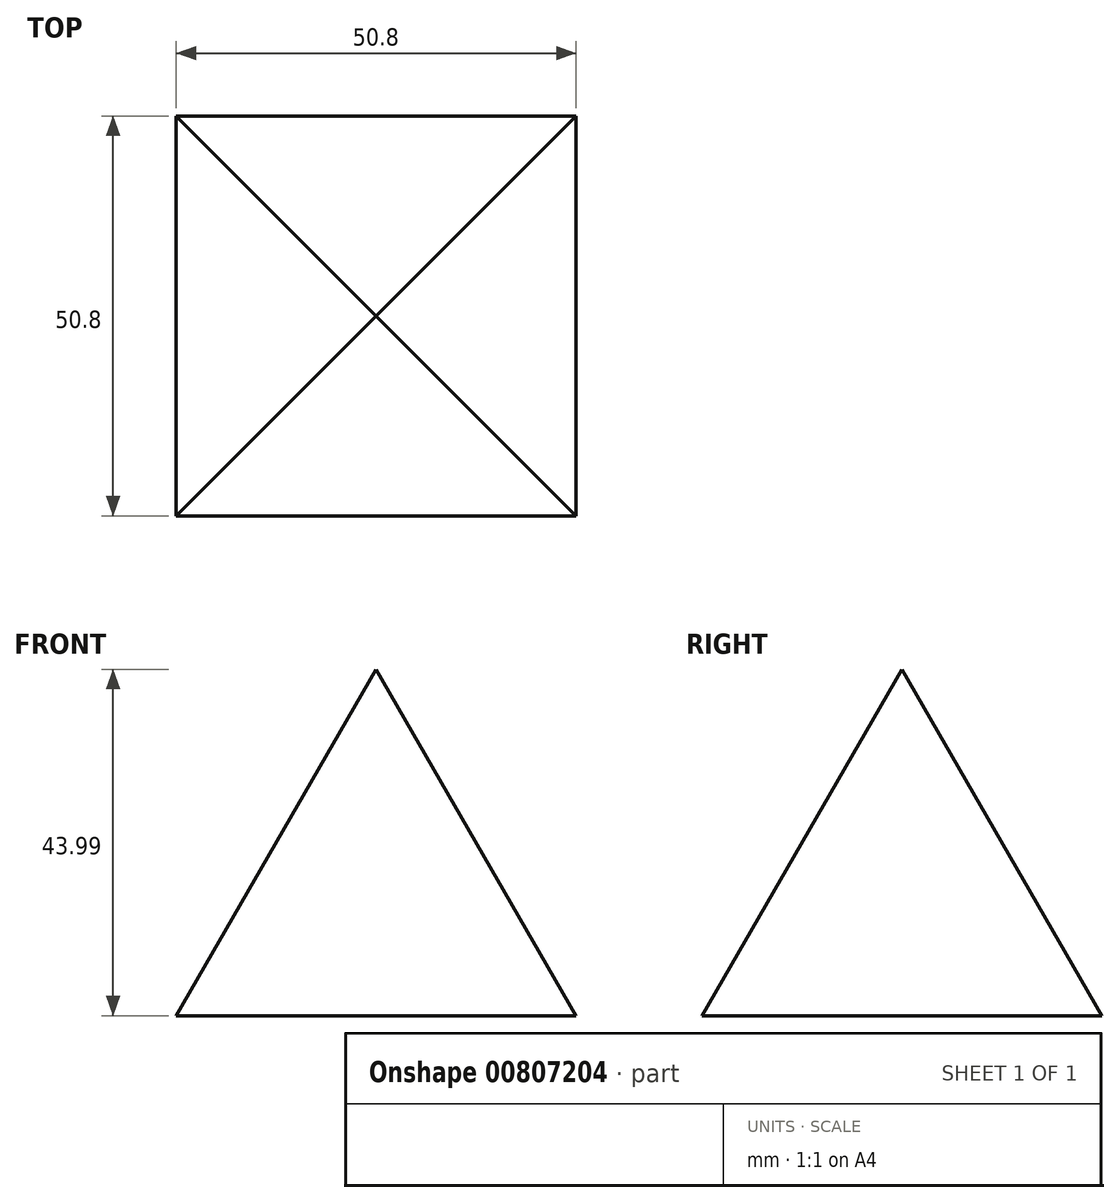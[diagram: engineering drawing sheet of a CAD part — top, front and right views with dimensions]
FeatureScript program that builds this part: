
annotation { "Feature Type Name" : "Feature", "Feature Type Description" : "" }
export const myFeature = defineFeature(function(context is Context, id is Id, definition is map)
    precondition{}
    {
        {
            var Q0;
            Q0=qCreatedBy(makeId("Top.planeOp"),FACE);
            var sketch = newSketch(context, id + "F0", { "sketchPlane" : qUnion([Q0])});
            skLineSegment(sketch, "E0.bottom", {"start": v(-33.35, 19.66) * mm, "end": v(17.45, 19.66) * mm});
            skLineSegment(sketch, "E0.top", {"start": v(-33.35, -31.14) * mm, "end": v(17.45, -31.14) * mm});
            skLineSegment(sketch, "E0.left", {"start": v(-33.35, 19.66) * mm, "end": v(-33.35, -31.14) * mm});
            skLineSegment(sketch, "E0.right", {"start": v(17.45, 19.66) * mm, "end": v(17.45, -31.14) * mm});
            skSolve(sketch);
        }
        {
            var Q0;
            Q0=makeQuery(id+"F0.imprint","IMPRINT",FACE,{"disambiguationData":[TD([[makeQuery(id+"F0.imprint","IMPRINT",EDGE,{"derivedFrom":sQuery(id+"F0.wireOp",EDGE,"E0.bottom")}),-1.0]])]});
            extrude(context, id + "F1", {"entities" : qUnion([Q0]), "depth" : 59.94 * mm, "offsetDistance" : 25.4 * mm, "hasDraft" : true, "draftAngle" : 30 * degree, "draftPullDirection" : true});
        }
    });
